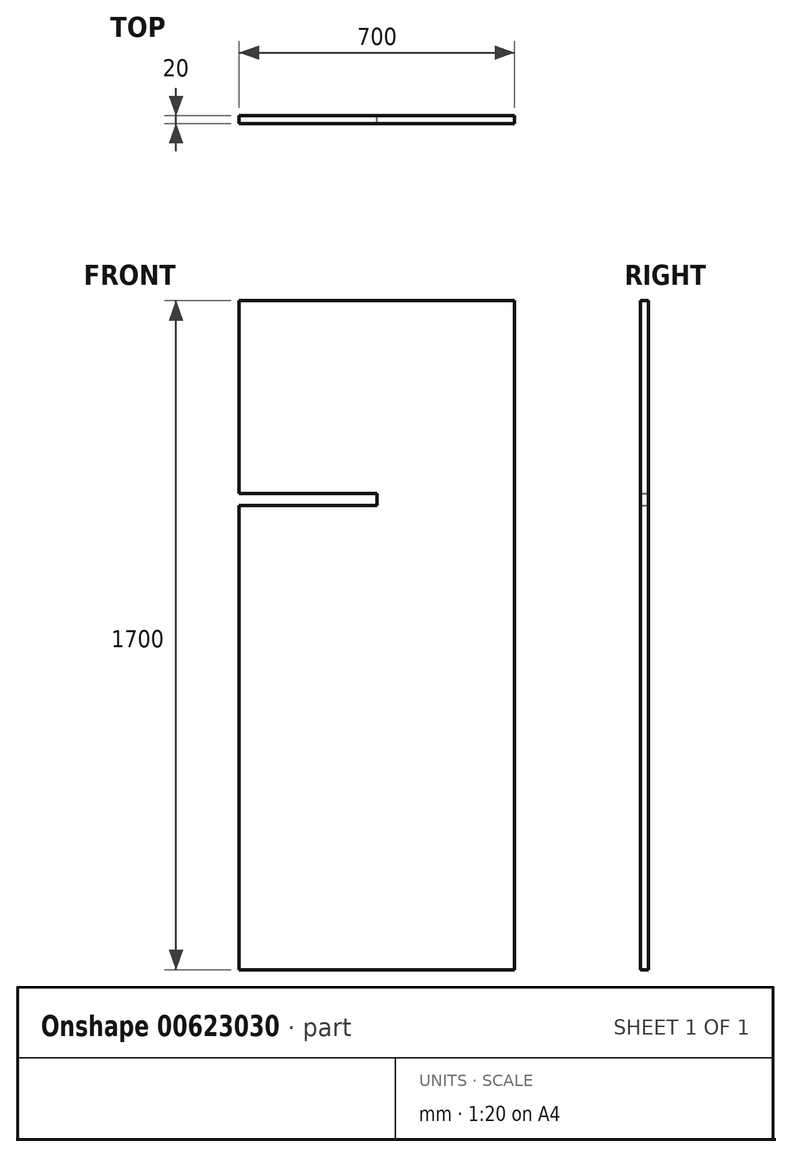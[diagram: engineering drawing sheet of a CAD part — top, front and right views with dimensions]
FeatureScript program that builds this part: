
annotation { "Feature Type Name" : "Feature", "Feature Type Description" : "" }
export const myFeature = defineFeature(function(context is Context, id is Id, definition is map)
    precondition{}
    {
        {
            var Q0;
            Q0=qCreatedBy(makeId("Front.planeOp"),FACE);
            var sketch = newSketch(context, id + "F0", { "sketchPlane" : qUnion([Q0])});
            skLineSegment(sketch, "E0.bottom", {"start": v(0, 0) * mm, "end": v(700, 0) * mm});
            skLineSegment(sketch, "E0.top", {"start": v(0, 1700) * mm, "end": v(700, 1700) * mm});
            skLineSegment(sketch, "E0.left", {"start": v(0, 0) * mm, "end": v(0, 1180) * mm});
            skLineSegment(sketch, "E0.right", {"start": v(700, 0) * mm, "end": v(700, 1700) * mm});
            skLineSegment(sketch, "E1", {"start": v(0, 1210) * mm, "end": v(350, 1210) * mm});
            skLineSegment(sketch, "E2", {"start": v(350, 1210) * mm, "end": v(350, 1180) * mm});
            skLineSegment(sketch, "E3", {"start": v(350, 1180) * mm, "end": v(0, 1180) * mm});
            skLineSegment(sketch, "E4.trimOffspring", {"start": v(0, 1210) * mm, "end": v(0, 1700) * mm});
            skSolve(sketch);
        }
        {
            var Q0;
            Q0 = qSketchRegion(id + "F0", true);
            extrude(context, id + "F1", {"entities" : qUnion([Q0]), "depth" : 20 * mm, "offsetDistance" : 25 * mm});
        }
    });
